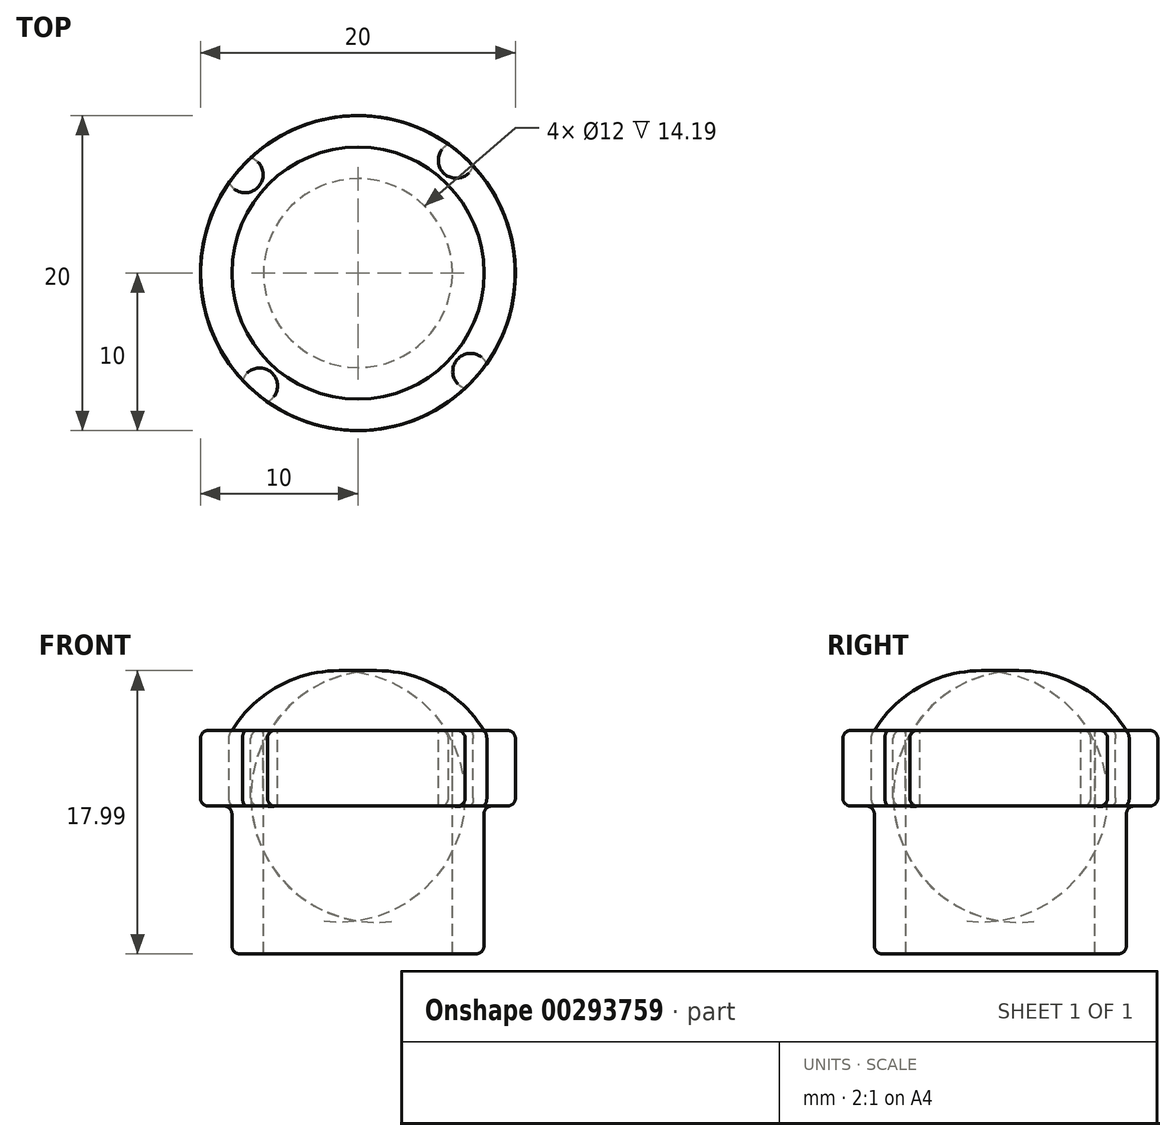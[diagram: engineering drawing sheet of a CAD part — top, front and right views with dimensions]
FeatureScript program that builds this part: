
annotation { "Feature Type Name" : "Feature", "Feature Type Description" : "" }
export const myFeature = defineFeature(function(context is Context, id is Id, definition is map)
    precondition{}
    {
        {
            var Q0;
            Q0=qCreatedBy(makeId("Front.planeOp"),FACE);
            var sketch = newSketch(context, id + "F0", { "sketchPlane" : qUnion([Q0])});
            skLineSegment(sketch, "E0", {"start": v(0, 0) * mm, "end": v(0, 29.7) * mm, "construction": true});
            skLineSegment(sketch, "E1", {"start": v(8, -3.7) * mm, "end": v(10, -3.7) * mm});
            skLineSegment(sketch, "E2", {"start": v(10, -3.7) * mm, "end": v(10, -8.5) * mm});
            skLineSegment(sketch, "E3", {"start": v(10, -8.5) * mm, "end": v(8, -8.5) * mm});
            skLineSegment(sketch, "E4", {"start": v(8, -8.5) * mm, "end": v(8, -17.9) * mm});
            skLineSegment(sketch, "E5", {"start": v(6, -17.9) * mm, "end": v(6, -3.7) * mm});
            skLineSegment(sketch, "E6", {"start": v(6, -3.7) * mm, "end": v(0, -3.7) * mm});
            skLineSegment(sketch, "E7", {"start": v(0, -3.7) * mm, "end": v(0, 0) * mm});
            skArc(sketch, "E8", {"start": v(8, -3.7) * mm, "mid": v(4.56, -0.65) * mm, "end": v(0, 0) * mm});
            skLineSegment(sketch, "E9", {"start": v(8, -17.9) * mm, "end": v(6, -17.9) * mm});
            skLineSegment(sketch, "E10", {"start": v(0, 0) * mm, "end": v(0, -19.89) * mm, "construction": true});
            skLineSegment(sketch, "E11", {"start": v(6, -17.9) * mm, "end": v(-10.75, -17.9) * mm, "construction": true});
            skPoint(sketch, "E12", {"position": v(0, -17.9) * mm});
            skSolve(sketch);
        }
        {
            var Q0;
            Q0=makeQuery(id+"F0.imprint","IMPRINT",FACE,{"disambiguationData":[TD([[makeQuery(id+"F0.imprint","IMPRINT",EDGE,{"derivedFrom":sQuery(id+"F0.wireOp",EDGE,"E1")}),-1.0]])]});
            var Q1;
            Q1=sQuery(id+"F0.wireOp",EDGE,"E10");
            revolve(context, id + "F1", {"entities" : qUnion([Q0]), "axis" : qUnion([Q1]), "revolveType" : RevolveType.FULL});
        }
        {
            var Q0;
            Q0=makeQuery(id+"F1.opRevolve","SWEPT_EDGE",EDGE,{"disambiguationData":[OSD([sQuery(id+"F0.wireOp",EDGE,"E1"),sQuery(id+"F0.wireOp",EDGE,"E2")])]});
            var Q1;
            Q1=makeQuery(id+"F1.opRevolve","SWEPT_EDGE",EDGE,{"disambiguationData":[OSD([sQuery(id+"F0.wireOp",EDGE,"E2"),sQuery(id+"F0.wireOp",EDGE,"E3")])]});
            var Q2;
            Q2=makeQuery(id+"F1.opRevolve","SWEPT_FACE",FACE,{"disambiguationData":[OSD([sQuery(id+"F0.wireOp",EDGE,"E4")])]});
            fillet(context, id + "F2", {"entities" : qUnion([Q0, Q1, Q2]), "radius" : .5 * mm, "tangentPropagation" : true, "allowEdgeOverflow" : false});
        }
        {
            var Q0;
            Q0=makeQuery(id+"F1.opRevolve","SWEPT_FACE",FACE,{"disambiguationData":[OSD([sQuery(id+"F0.wireOp",EDGE,"E1")])]});
            var sketch = newSketch(context, id + "F3", { "sketchPlane" : qUnion([Q0])});
            skCircle(sketch, "E13", {"center": v(7.16, -6.24) * mm, "radius": 1.14 * mm});
            skSolve(sketch);
        }
        {
            var Q0;
            {var subQ0=sQuery(id+"F3.wireOp",EDGE,"E13");var subQ1=sQuery(id+"F0.wireOp",EDGE,"E1");var subQ2=makeQuery(id+"F2.opFillet","BLEND_EDGE",EDGE,{"blendedFrom":[makeQuery(id+"F1.opRevolve","SWEPT_EDGE",EDGE,{"disambiguationData":[OSD([subQ1,sQuery(id+"F0.wireOp",EDGE,"E2")])]}),makeQuery(id+"F1.opRevolve","SWEPT_FACE",FACE,{"disambiguationData":[OSD([subQ1])]})],"blendedInto":[makeQuery(id+"F1.opRevolve","SWEPT_FACE",FACE,{"disambiguationData":[OSD([subQ1])]})]});var subQ3=makeQuery(id+"F3.imprint","INTERSECT",VERTEX,{"disambiguationData":[OD(0.0)],"derivedFrom":[subQ2,subQ0]});Q0=makeQuery(id+"F3.imprint","IMPRINT",FACE,{"disambiguationData":[TD([[makeQuery(id+"F3.imprint","IMPRINT",EDGE,{"disambiguationData":[TD([[subQ3,-1.0]])],"derivedFrom":subQ0}),1.0]])]});}
            var Q1;
            {var subQ0=sQuery(id+"F3.wireOp",EDGE,"E13");var subQ1=sQuery(id+"F0.wireOp",EDGE,"E1");var subQ2=makeQuery(id+"F2.opFillet","BLEND_EDGE",EDGE,{"blendedFrom":[makeQuery(id+"F1.opRevolve","SWEPT_EDGE",EDGE,{"disambiguationData":[OSD([subQ1,sQuery(id+"F0.wireOp",EDGE,"E2")])]}),makeQuery(id+"F1.opRevolve","SWEPT_FACE",FACE,{"disambiguationData":[OSD([subQ1])]})],"blendedInto":[makeQuery(id+"F1.opRevolve","SWEPT_FACE",FACE,{"disambiguationData":[OSD([subQ1])]})]});var subQ3=makeQuery(id+"F3.imprint","INTERSECT",VERTEX,{"disambiguationData":[OD(0.0)],"derivedFrom":[subQ2,subQ0]});Q1=makeQuery(id+"F3.imprint","IMPRINT",FACE,{"disambiguationData":[TD([[makeQuery(id+"F3.imprint","IMPRINT",EDGE,{"disambiguationData":[TD([[subQ3,1.0]])],"derivedFrom":subQ0}),1.0]])]});}
            extrude(context, id + "F4", {"entities" : qUnion([Q0, Q1]), "operationType" : NewBodyOperationType.REMOVE, "oppositeDirection" : true, "depth" : 25 * mm});
        }
        {
            var Q0;
            Q0=makeQuery(id+"F1.opRevolve","SWEPT_BODY",BODY,{"disambiguationData":[OSD([sQuery(id+"F0.wireOp",EDGE,"E1"),sQuery(id+"F0.wireOp",EDGE,"E2"),sQuery(id+"F0.wireOp",EDGE,"E3"),sQuery(id+"F0.wireOp",EDGE,"E4"),sQuery(id+"F0.wireOp",EDGE,"E5"),sQuery(id+"F0.wireOp",EDGE,"E6"),sQuery(id+"F0.wireOp",EDGE,"E7"),sQuery(id+"F0.wireOp",EDGE,"E8"),sQuery(id+"F0.wireOp",EDGE,"E9")])]});
            var Q1;
            Q1=makeQuery(id+"F1.opRevolve","SWEPT_EDGE",EDGE,{"disambiguationData":[OSD([sQuery(id+"F0.wireOp",EDGE,"E1"),sQuery(id+"F0.wireOp",EDGE,"E8")])]});
            circularPattern(context, id + "F5", {"entities" : qUnion([Q0]), "axis" : qUnion([Q1]), "angle" : 360 * degree, "instanceCount" : 4, "equalSpace" : true});
        }
    });
